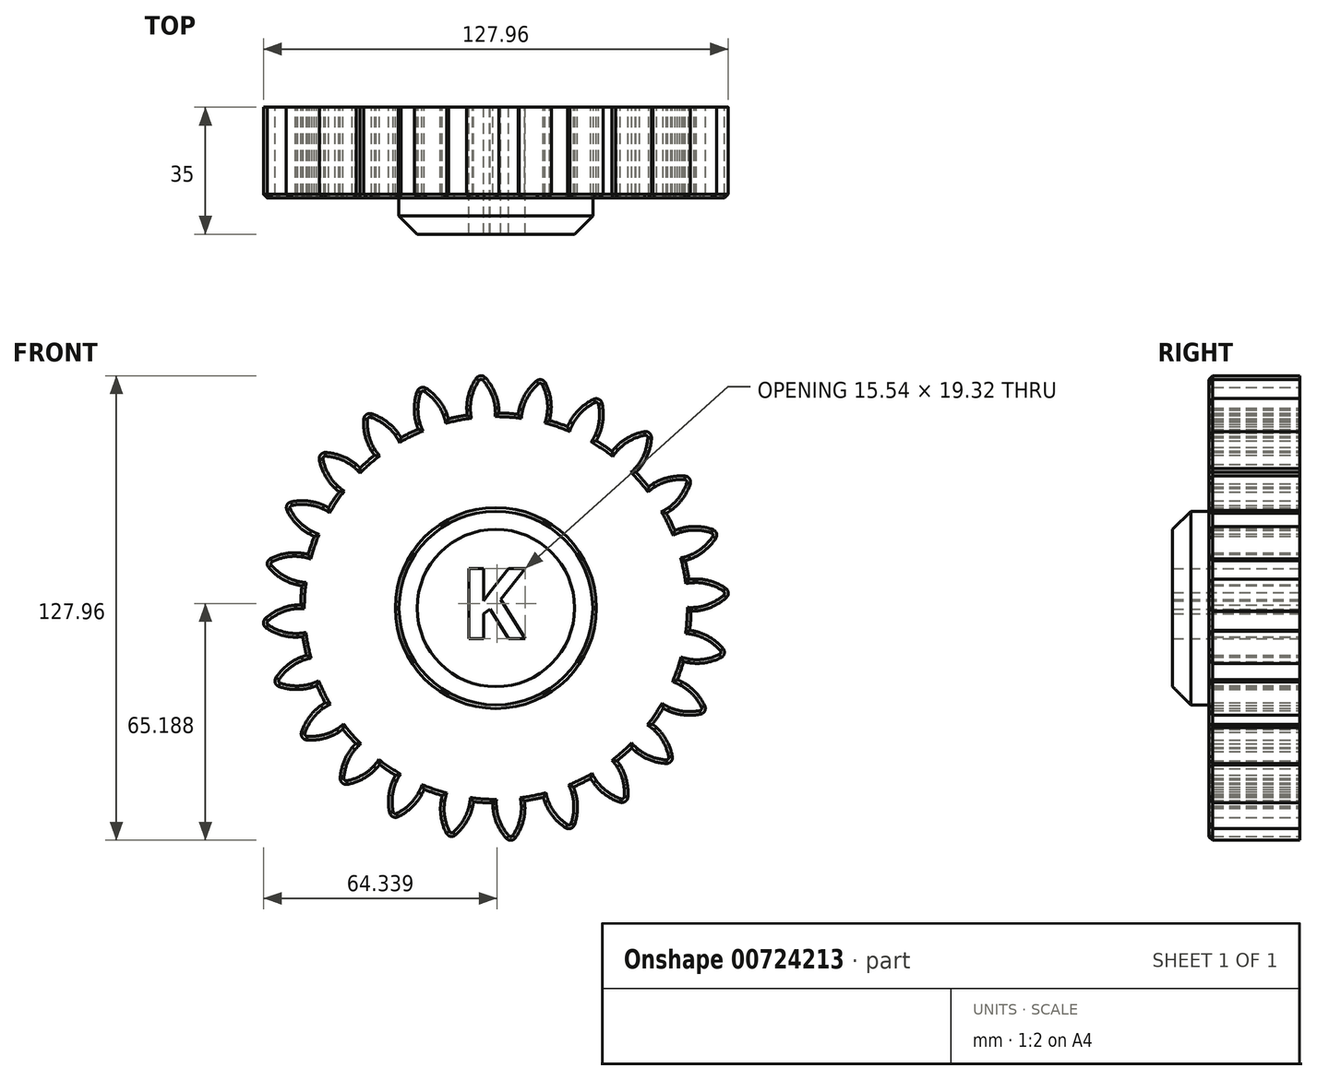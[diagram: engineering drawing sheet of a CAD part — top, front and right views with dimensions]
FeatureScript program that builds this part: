
annotation { "Feature Type Name" : "Feature", "Feature Type Description" : "" }
export const myFeature = defineFeature(function(context is Context, id is Id, definition is map)
    precondition{}
    {
        {
            var Q0;
            Q0=qCreatedBy(makeId("Front.planeOp"),FACE);
            var sketch = newSketch(context, id + "F0", { "sketchPlane" : qUnion([Q0])});
            skCircle(sketch, "E0", {"center": v(0, 0) * mm, "radius": 53.72 * mm});
            skCircle(sketch, "E1", {"center": v(0, 0) * mm, "radius": 58.67 * mm, "construction": true});
            skCircle(sketch, "E2", {"center": v(0, 0) * mm, "radius": 63.5 * mm, "construction": true});
            skLineSegment(sketch, "E3", {"start": v(0, 0) * mm, "end": v(0, 75.31) * mm, "construction": true});
            skLineSegment(sketch, "E4", {"start": v(0, 0) * mm, "end": v(-4.94, 75.31) * mm, "construction": true});
            skLineSegment(sketch, "E5", {"start": v(0, 58.67) * mm, "end": v(-66.03, 58.67) * mm, "construction": true});
            skLineSegment(sketch, "E6", {"start": v(0, 58.67) * mm, "end": v(-58.84, 37.26) * mm, "construction": true});
            skCircle(sketch, "E7", {"center": v(0, 0) * mm, "radius": 55.14 * mm, "construction": true});
            skCircle(sketch, "E8", {"center": v(0, 58.67) * mm, "radius": 14.6 * mm, "construction": true});
            skCircle(sketch, "E9", {"center": v(-13.72, 53.68) * mm, "radius": 14.6 * mm, "construction": true});
            skArc(sketch, "E10", {"start": v(0, 58.67) * mm, "mid": v(-1.2, 61.19) * mm, "end": v(-2.86, 63.44) * mm});
            skArc(sketch, "E11", {"start": v(0.8, 55.13) * mm, "mid": v(0.52, 56.93) * mm, "end": v(0, 58.67) * mm});
            skArc(sketch, "E12", {"start": v(0.88, 53.71) * mm, "mid": v(0.86, 54.42) * mm, "end": v(0.8, 55.13) * mm});
            skArc(sketch, "E13.MirrorCS", {"start": v(-7.66, 58.17) * mm, "mid": v(-6.79, 60.82) * mm, "end": v(-5.45, 63.27) * mm});
            skArc(sketch, "E14.MirrorCS", {"start": v(-8, 54.55) * mm, "mid": v(-7.95, 56.37) * mm, "end": v(-7.66, 58.17) * mm});
            skArc(sketch, "E15", {"start": v(-2.86, 63.44) * mm, "mid": v(-4.2, 63.98) * mm, "end": v(-5.45, 63.27) * mm});
            skArc(sketch, "E16.MirrorCS", {"start": v(-7.88, 53.14) * mm, "mid": v(-7.96, 53.84) * mm, "end": v(-8, 54.55) * mm});
            skCircle(sketch, "E17", {"center": v(0, 0) * mm, "radius": 26.67 * mm});
            skText(sketch, "E18", { "text": "K", "fontName": "OpenSans-Bold.ttf"});
            const initialGuessF0  = {"E18": [-0.00984, -0.00845, 1, 0, 0.01948]};
            skSetInitialGuess(sketch, initialGuessF0);
            skSolve(sketch);
        }
        {
            var Q0;
            {var subQ0=sQuery(id+"F0.wireOp",EDGE,"E0");var subQ1=makeQuery(id+"F0.imprint","INTERSECT",VERTEX,{"derivedFrom":[subQ0,sQuery(id+"F0.wireOp",EDGE,"E12")]});Q0=makeQuery(id+"F0.imprint","IMPRINT",FACE,{"disambiguationData":[TD([[makeQuery(id+"F0.imprint","IMPRINT",EDGE,{"disambiguationData":[TD([[subQ1,-1.0]])],"derivedFrom":subQ0}),1.0]])]});}
            var Q1;
            Q1=makeQuery(id+"F0.imprint","IMPRINT",FACE,{"disambiguationData":[TD([[makeQuery(id+"F0.imprint","IMPRINT",EDGE,{"derivedFrom":sQuery(id+"F0.wireOp",EDGE,"E10")}),1.0]])]});
            extrude(context, id + "F1", {"entities" : qUnion([Q0, Q1]), "depth" : 25 * mm, "offsetDistance" : 25 * mm});
        }
        {
            var Q0;
            Q0=makeQuery(id+"F1.opExtrude","CAP_EDGE",EDGE,{"disambiguationData":[OSD([sQuery(id+"F0.wireOp",EDGE,"E0")])],"isStart":false});
            var Q1;
            Q1=makeQuery(id+"F1.opExtrude","CAP_EDGE",EDGE,{"disambiguationData":[OSD([sQuery(id+"F0.wireOp",EDGE,"E10")])],"isStart":false});
            var Q2;
            Q2=makeQuery(id+"F1.opExtrude","CAP_EDGE",EDGE,{"disambiguationData":[OSD([sQuery(id+"F0.wireOp",EDGE,"E14.MirrorCS")])],"isStart":false});
            var Q3;
            Q3=makeQuery(id+"F1.opExtrude","CAP_FACE",FACE,{"disambiguationData":[OSD([sQuery(id+"F0.wireOp",EDGE,"E0"),sQuery(id+"F0.wireOp",EDGE,"E10"),sQuery(id+"F0.wireOp",EDGE,"E11"),sQuery(id+"F0.wireOp",EDGE,"E12"),sQuery(id+"F0.wireOp",EDGE,"E13.MirrorCS"),sQuery(id+"F0.wireOp",EDGE,"E14.MirrorCS"),sQuery(id+"F0.wireOp",EDGE,"E15"),sQuery(id+"F0.wireOp",EDGE,"E16.MirrorCS"),sQuery(id+"F0.wireOp",EDGE,"E17")])],"isStart":false});
            chamfer(context, id + "F2", {"entities" : qUnion([Q0, Q1, Q2, Q3]), "width" : 1 * mm, "tangentPropagation" : true});
        }
        {
            var Q0;
            Q0=makeQuery(id+"F1.opExtrude","SWEPT_BODY",BODY,{"disambiguationData":[OSD([sQuery(id+"F0.wireOp",EDGE,"E0"),sQuery(id+"F0.wireOp",EDGE,"E10"),sQuery(id+"F0.wireOp",EDGE,"E11"),sQuery(id+"F0.wireOp",EDGE,"E12"),sQuery(id+"F0.wireOp",EDGE,"E13.MirrorCS"),sQuery(id+"F0.wireOp",EDGE,"E14.MirrorCS"),sQuery(id+"F0.wireOp",EDGE,"E15"),sQuery(id+"F0.wireOp",EDGE,"E16.MirrorCS"),sQuery(id+"F0.wireOp",EDGE,"E17")])]});
            var Q1;
            Q1=makeQuery(id+"F1.opExtrude","SWEPT_FACE",FACE,{"disambiguationData":[OSD([sQuery(id+"F0.wireOp",EDGE,"E0")])]});
            circularPattern(context, id + "F3", {"entities" : qUnion([Q0]), "axis" : qUnion([Q1]), "angle" : 360 * degree, "instanceCount" : 24, "equalSpace" : true});
        }
        {
            var Q0;
            Q0=makeQuery(id+"F0.imprint","IMPRINT",FACE,{"disambiguationData":[TD([[makeQuery(id+"F0.imprint","IMPRINT",EDGE,{"derivedFrom":sQuery(id+"F0.wireOp",EDGE,"E17")}),1.0]])]});
            extrude(context, id + "F4", {"entities" : qUnion([Q0]), "operationType" : NewBodyOperationType.ADD, "depth" : 35 * mm, "offsetDistance" : 25 * mm});
        }
        {
            var Q0;
            Q0=makeQuery(id+"F4.opExtrude","CAP_EDGE",EDGE,{"disambiguationData":[OSD([sQuery(id+"F0.wireOp",EDGE,"E17")])],"isStart":false});
            chamfer(context, id + "F5", {"entities" : qUnion([Q0]), "width" : 5 * mm, "tangentPropagation" : true});
        }
    });
